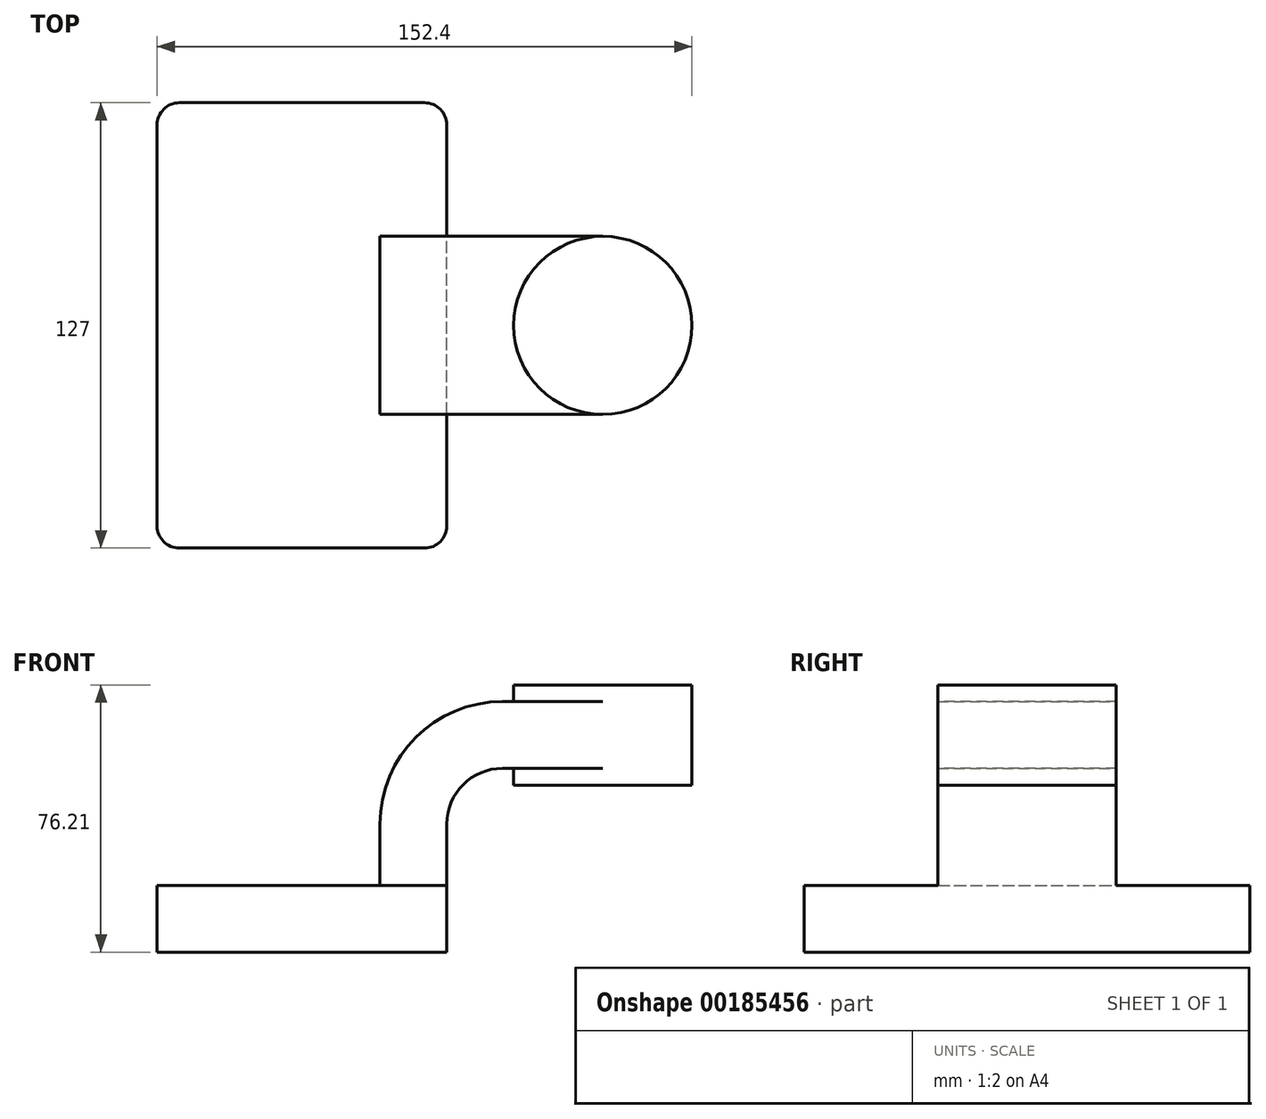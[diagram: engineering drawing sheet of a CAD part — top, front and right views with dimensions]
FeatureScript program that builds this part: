
annotation { "Feature Type Name" : "Feature", "Feature Type Description" : "" }
export const myFeature = defineFeature(function(context is Context, id is Id, definition is map)
    precondition{}
    {
        {
            var Q0;
            Q0=qCreatedBy(makeId("Front.planeOp"),FACE);
            var sketch = newSketch(context, id + "F0", { "sketchPlane" : qUnion([Q0])});
            skLineSegment(sketch, "E0.bottom", {"start": v(41.27, 9.53) * mm, "end": v(-41.28, 9.53) * mm});
            skLineSegment(sketch, "E0.top", {"start": v(41.28, -9.52) * mm, "end": v(-41.27, -9.52) * mm});
            skLineSegment(sketch, "E0.left", {"start": v(41.27, 9.53) * mm, "end": v(41.28, -9.52) * mm});
            skLineSegment(sketch, "E0.right", {"start": v(-41.28, 9.53) * mm, "end": v(-41.27, -9.52) * mm});
            skPoint(sketch, "E0.middle", {"position": v(0, 0) * mm});
            skLineSegment(sketch, "E1.bottom", {"start": v(111.12, 66.68) * mm, "end": v(60.32, 66.68) * mm});
            skLineSegment(sketch, "E1.top", {"start": v(111.12, 38.1) * mm, "end": v(60.32, 38.1) * mm});
            skLineSegment(sketch, "E1.left", {"start": v(111.12, 66.68) * mm, "end": v(111.12, 38.1) * mm});
            skLineSegment(sketch, "E1.right", {"start": v(60.32, 66.68) * mm, "end": v(60.32, 38.1) * mm});
            skPoint(sketch, "E1.middle", {"position": v(85.72, 52.39) * mm});
            skLineSegment(sketch, "E2", {"start": v(41.27, 9.53) * mm, "end": v(41.27, 27) * mm});
            skArc(sketch, "E3", {"start": v(41.27, 27) * mm, "mid": v(45.92, 38.23) * mm, "end": v(57.15, 42.88) * mm});
            skLineSegment(sketch, "E4", {"start": v(57.15, 42.88) * mm, "end": v(85.72, 42.88) * mm});
            skLineSegment(sketch, "E5.0", {"start": v(57.15, 61.93) * mm, "end": v(85.72, 61.93) * mm});
            skArc(sketch, "E5.1", {"start": v(22.22, 27) * mm, "mid": v(32.45, 51.7) * mm, "end": v(57.15, 61.93) * mm});
            skLineSegment(sketch, "E5.2", {"start": v(22.22, 9.53) * mm, "end": v(22.22, 27) * mm});
            skFitSpline(sketch, "E6", {"points": [v(-41.28, 9.53) * mm, v(57.15, 61.93) * mm], "startDerivative": vector(145.47, 22.2) * mm, "endDerivative": vector(139.18, -14.48) * mm});
            skPoint(sketch, "E7", {"position": v(85.72, 66.68) * mm});
            skLineSegment(sketch, "E8", {"start": v(85.72, 66.68) * mm, "end": v(85.72, 38.1) * mm});
            skSolve(sketch);
        }
        {
            var Q0;
            Q0=makeQuery(id+"F0.imprint","IMPRINT",FACE,{"disambiguationData":[TD([[makeQuery(id+"F0.imprint","IMPRINT",EDGE,{"derivedFrom":sQuery(id+"F0.wireOp",EDGE,"E0.top")}),-1.0]])]});
            extrude(context, id + "F1", {"entities" : qUnion([Q0]), "endBound" : BoundingType.SYMMETRIC, "depth" : 127 * mm});
        }
        {
            var Q0;
            {var subQ5=sQuery(id+"F0.wireOp",EDGE,"0AODHszc-27tY-CVQi-S3WZ-xXC0kvkR7iSj");Q0=makeQuery(id+"F0.imprint","IMPRINT",FACE,{"disambiguationData":[TD([[makeQuery(id+"F0.imprint","IMPRINT",EDGE,{"derivedFrom":subQ5}),1.0]])]});}
            var Q1;
            {var subQ1=sQuery(id+"F0.wireOp",EDGE,"E2");Q1=makeQuery(id+"F0.imprint","IMPRINT",FACE,{"disambiguationData":[TD([[makeQuery(id+"F0.imprint","IMPRINT",EDGE,{"derivedFrom":subQ1}),1.0]])]});}
            var Q2;
            {var subQ0=sQuery(id+"F0.wireOp",EDGE,"E5.0");var subQ1=sQuery(id+"F0.wireOp",EDGE,"E1.right");var subQ2=makeQuery(id+"F0.imprint","INTERSECT",VERTEX,{"derivedFrom":[subQ1,subQ0]});Q2=makeQuery(id+"F0.imprint","IMPRINT",FACE,{"disambiguationData":[TD([[makeQuery(id+"F0.imprint","IMPRINT",EDGE,{"disambiguationData":[TD([[subQ2,-1.0]])],"derivedFrom":subQ1}),1.0]])]});}
            extrude(context, id + "F2", {"entities" : qUnion([Q0, Q1, Q2]), "operationType" : NewBodyOperationType.ADD, "endBound" : BoundingType.SYMMETRIC, "depth" : 50.8 * mm});
        }
        {
            var Q0;
            Q0=makeQuery(id+"F0.imprint","IMPRINT",FACE,{"disambiguationData":[TD([[makeQuery(id+"F0.imprint","IMPRINT",EDGE,{"derivedFrom":sQuery(id+"F0.wireOp",EDGE,"E5.1")}),1.0]])]});
            extrude(context, id + "F3", {"entities" : qUnion([Q0]), "operationType" : NewBodyOperationType.ADD, "endBound" : BoundingType.SYMMETRIC, "depth" : 15.88 * mm});
        }
        {
            var Q0;
            {var subQ0=sQuery(id+"F0.wireOp",EDGE,"E1.left");Q0=makeQuery(id+"F0.imprint","IMPRINT",FACE,{"disambiguationData":[TD([[makeQuery(id+"F0.imprint","IMPRINT",EDGE,{"derivedFrom":subQ0}),-1.0]])]});}
            var Q1;
            Q1=sQuery(id+"F0.wireOp",EDGE,"E8");
            revolve(context, id + "F4", {"operationType" : NewBodyOperationType.ADD, "entities" : qUnion([Q0]), "axis" : qUnion([Q1]), "revolveType" : RevolveType.FULL});
        }
        {
            var Q0;
            Q0=makeQuery(id+"F1.opExtrude","CAP_EDGE",EDGE,{"disambiguationData":[OSD([sQuery(id+"F0.wireOp",EDGE,"E0.left")])],"isStart":false});
            var Q1;
            Q1=makeQuery(id+"F1.opExtrude","CAP_EDGE",EDGE,{"disambiguationData":[OSD([sQuery(id+"F0.wireOp",EDGE,"E0.right")])],"isStart":false});
            var Q2;
            Q2=makeQuery(id+"F1.opExtrude","CAP_EDGE",EDGE,{"disambiguationData":[OSD([sQuery(id+"F0.wireOp",EDGE,"E0.left")])],"isStart":true});
            var Q3;
            Q3=makeQuery(id+"F1.opExtrude","CAP_EDGE",EDGE,{"disambiguationData":[OSD([sQuery(id+"F0.wireOp",EDGE,"E0.right")])],"isStart":true});
            fillet(context, id + "F5", {"entities" : qUnion([Q0, Q1, Q2, Q3]), "radius" : 6.35 * mm, "tangentPropagation" : true, "allowEdgeOverflow" : false});
        }
    });
